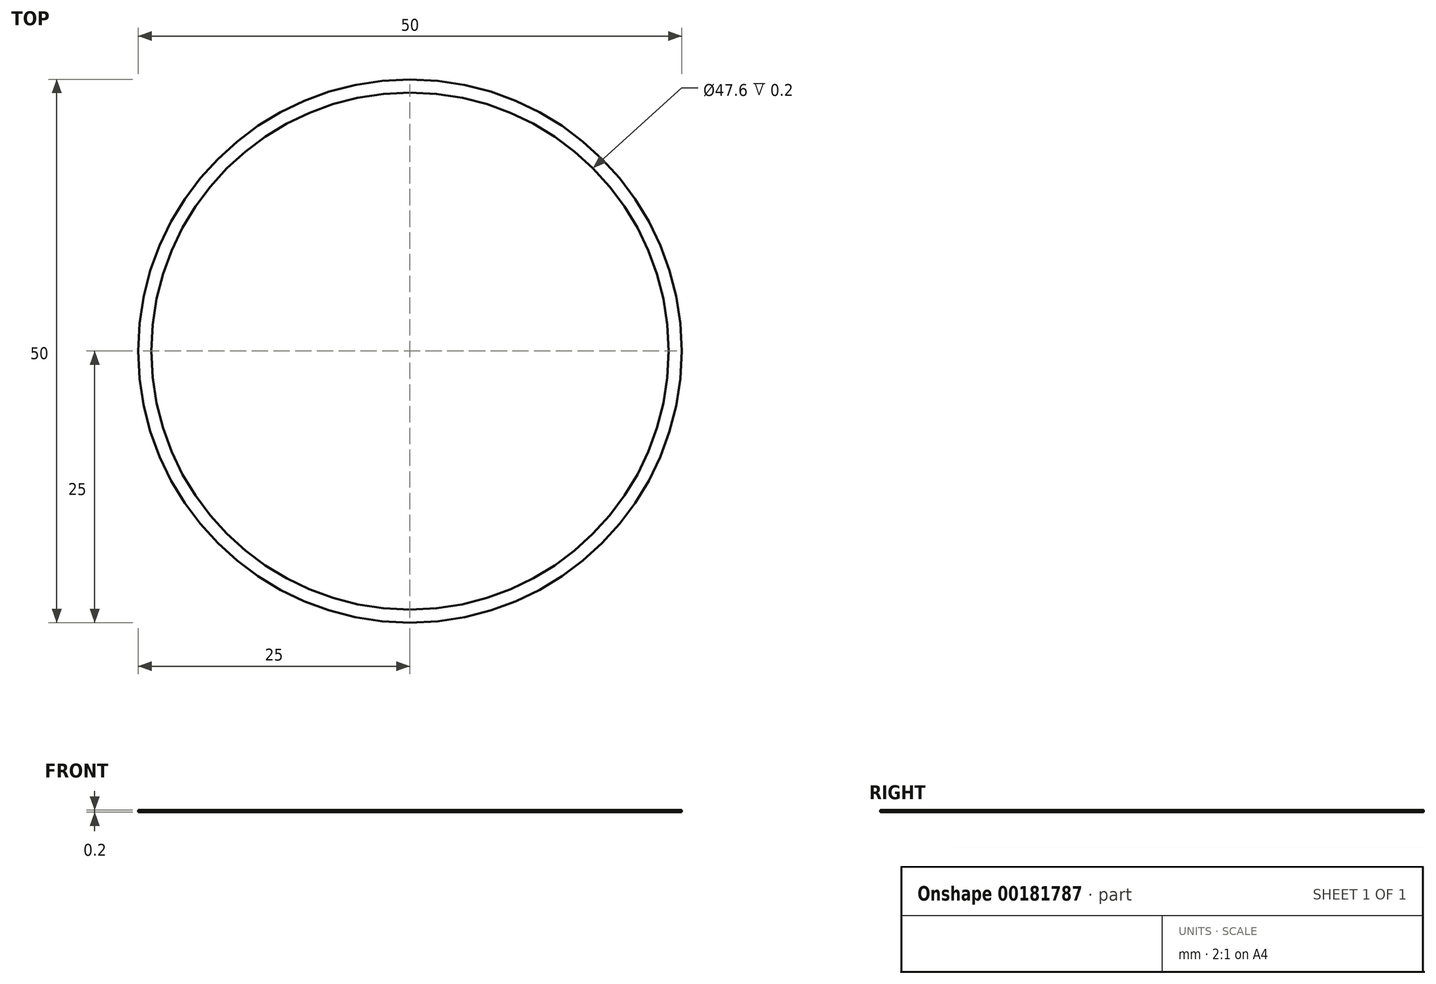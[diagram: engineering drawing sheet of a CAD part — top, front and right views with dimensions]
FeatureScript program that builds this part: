
annotation { "Feature Type Name" : "Feature", "Feature Type Description" : "" }
export const myFeature = defineFeature(function(context is Context, id is Id, definition is map)
    precondition{}
    {
        {
            var Q0;
            Q0=qCreatedBy(makeId("Top.planeOp"),FACE);
            var sketch = newSketch(context, id + "F0", { "sketchPlane" : qUnion([Q0])});
            skCircle(sketch, "E0", {"center": v(0, 0) * mm, "radius": 25 * mm});
            skCircle(sketch, "E1.0", {"center": v(0, 0) * mm, "radius": 23.8 * mm});
            skSolve(sketch);
        }
        {
            var Q0;
            Q0 = qSketchRegion(id + "F0", true);
            extrude(context, id + "F1", {"entities" : qUnion([Q0]), "depth" : 0.2 * mm});
        }
    });
